# Revit family: VLN_NimbusMedical_B9478_BIM_NL
name_source: partatom
category: Plumbing Fixtures
revit_build: Autodesk Revit MEP 2014 (Build: 20140709_2115(x64)
units: mm (PartAtom-declared; Revit-internal decimal feet)

## types (1)
- B9478AA-NIM-MED WASTAFELMENGKR OPEN GREEP 170MM
    Afmetingen = 56 x 233 x 185 mm
    Afstands eenheid = millimeter
    Afwerking = Chroom
    Artikelnummer = B9478AA
    Artikelomschrijving = NIM-MED WASTAFELMENGKR OPEN GREEP 170MM
    Artikelreferentie = CeraPlus wastafelmengkraan DN 15 met lange open greep. Vaste uitloop met straalregelaar. Sprong 116 mm. Hoogte uitloop 73 mm. Flexibele aansluitslangen G3/8". Metalen greep. Onderbevestiging (EASY FIX). CLICK-cartouche met keramische schijven. Bevestiginggreep op de cartouche d.m.v. een RVS overbrengingspen. Draaibereik 120°. Geïntegreerd vetreservoir. ECO-functie (50% volumestop en drukafhankelijke temperatuur instelling). Uithoudingstest EN 817. Geluidsniveau volgens norm DIN 4109, Groep 1.

Kraan is zonder waste of ketting.
    Assembly Code = C1030200
    BIM Object Naam = Wastafelmengkraan
    BREEAMApproved = No
    BarCode = 3800861022053
    Bedieningswijze = Open greep
    Bedieningswijze kraan = Open greep
    CWFU = 0
    Cost = 0 $
    Default Elevation = 800 mm  [stored 2.62467 ft]
    Description = CeraPlus wastafelmengkraan DN 15 met lange open greep. Vaste uitloop met straalregelaar. Sprong 116 mm. Hoogte uitloop 73 mm. Flexibele aansluitslangen G3/8". Metalen greep. Onderbevestiging (EASY FIX). CLICK-cartouche met keramische schijven. Bevestiginggreep op de cartouche d.m.v. een RVS overbrengingspen. Draaibereik 120°. Geïntegreerd vetreservoir. ECO-functie (50% volumestop en drukafhankelijke temperatuur instelling). Uithoudingstest EN 817. Geluidsniveau volgens norm DIN 4109, Groep 1.

Kraan is zonder waste of ketting.
    Duur eenheid = jaar
    ECA = No
    Fabrieks URL = http://www.idealstandardnederland.nl
    Fabrieksgarantie = Fabrieksgarantie
    Fabrikant = Ideal Standard Nederland BV
    Garantieduur  eenheid = jaar
    Garantieduur onderdelen = 5
    Gemaakt op = 2014-10-10
    HWFU = 0
    IfcExportAs = IfcValveType
    IfcExportType = FAUCET
    Installatie instructies = http://www.idealstandardnederland.nl
    Kenmerken = Wastafelmengkraan DN 15 met lange open greep. Vaste uitloop met straalregelaar. Sprong 116 mm. Hoogte uitloop 73 mm. Flexibele aansluitslangen G3/8". Metalen greep. Onderbevestiging (EASY FIX). CLICK-cartouche met keramische schijven. Bevestiginggreep op de cartouche d.m.v. een RVS overbrengingspen. Draaibereik 120°. Geïntegreerd vetreservoir. ECO-functie (50% volumestop en drukafhankelijke temperatuur instelling). Uithoudingstest EN 817. Geluidsniveau volgens norm DIN 4109, Groep 1.

Kraan is zonder waste of ketting.
    Klepmechanisme = Keramische schijven
    Kleur = Chroom
    Materiaal = Messing
    Merk = Venlo
    Model = B9478AA
    NBSReference = 45-35-70/???
    Netto gewicht = 1,665 kg
    Nominale Breedte = 56 mm
    Nominale Hoogte = 185 mm
    Nominale Lengte = 233 mm
    Oppervlakte eenheid = millimeter
    Prestatie code = EN 817, DIN 4109
    Product soort = vast
    Productinformatie = http://www.idealstandardnederland.nl
    Reserve delen = www.idealstandardnederland.nl
    TMV3 = No
    Telefoonnummer = 31 (0) 77 355 08 08
    Testdruk = 10 Bar
    Toebehoren = www.idealstandardnederland.nl
    Toepassing = Intern
    Type kraan = Wastafelmengkraan
    Type montage = Sanitair
    URL = www.idealstandardnederland.nl
    Uniclass2 = Pr_40_20_87_98
    Versie = 1
    Verwachte levensduur = 25
    Volume eenheid = Liter
    Volumedoorstroom = ?L/hr @ ?bar
    Vorm = Gesculptuurd
    WFU = 0
    WRAS = Yes
    WaterEfficientProduct = No
    Waterdruk = 1-5 bar
    Werkwijze kraan = Mengkraan

note: [stored X ft] marks values corroborated as IEEE doubles in the binary element streams (Revit-internal decimal feet)

## geometry (parser evidence)
native form markers: Sweep x2
no freeform markers — native parametric forms only
